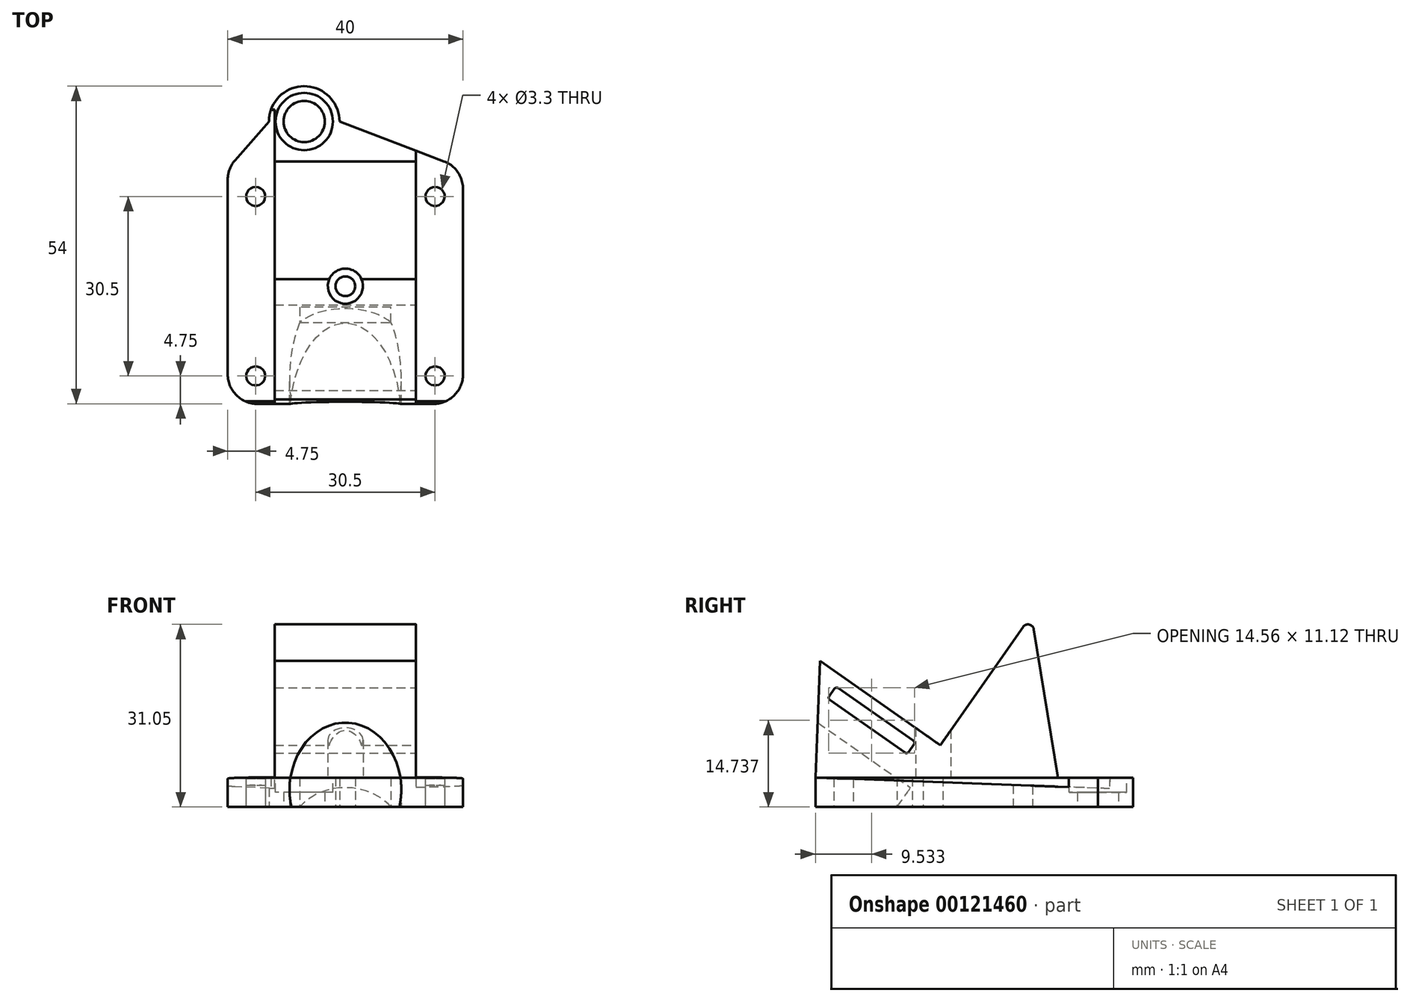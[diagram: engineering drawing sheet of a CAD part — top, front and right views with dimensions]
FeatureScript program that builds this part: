
annotation { "Feature Type Name" : "Feature", "Feature Type Description" : "" }
export const myFeature = defineFeature(function(context is Context, id is Id, definition is map)
    precondition{}
    {
        {
            var Q0;
            Q0=qCreatedBy(makeId("Top.planeOp"),FACE);
            var sketch = newSketch(context, id + "F0", { "sketchPlane" : qUnion([Q0])});
            skLineSegment(sketch, "E0.bottom", {"start": v(15.25, -15.25) * mm, "end": v(-15.25, -15.25) * mm, "construction": true});
            skLineSegment(sketch, "E0.top", {"start": v(15.25, 15.25) * mm, "end": v(-15.25, 15.25) * mm, "construction": true});
            skLineSegment(sketch, "E0.left", {"start": v(15.25, -15.25) * mm, "end": v(15.25, 15.25) * mm, "construction": true});
            skLineSegment(sketch, "E0.right", {"start": v(-15.25, -15.25) * mm, "end": v(-15.25, 15.25) * mm, "construction": true});
            skPoint(sketch, "E0.middle", {"position": v(0, 0) * mm});
            skCircle(sketch, "E1", {"center": v(-15.25, 15.25) * mm, "radius": 1.65 * mm});
            skCircle(sketch, "E2", {"center": v(15.25, 15.25) * mm, "radius": 1.65 * mm});
            skCircle(sketch, "E3", {"center": v(15.25, -15.25) * mm, "radius": 1.65 * mm});
            skCircle(sketch, "E4", {"center": v(-15.25, -15.25) * mm, "radius": 1.65 * mm});
            skLineSegment(sketch, "E5.bottom", {"start": v(15, -20) * mm, "end": v(-15, -20) * mm});
            skLineSegment(sketch, "E5.top", {"start": v(20, 20) * mm, "end": v(-20, 20) * mm});
            skLineSegment(sketch, "E5.left", {"start": v(20, -15) * mm, "end": v(20, 16.55) * mm});
            skLineSegment(sketch, "E5.right", {"start": v(-20, -15) * mm, "end": v(-20, 18.12) * mm});
            skCircle(sketch, "E6", {"center": v(-7, 28) * mm, "radius": 3.5 * mm});
            skPoint(sketch, "E6.centerSnap0", {"position": v(0, 20) * mm});
            skCircle(sketch, "E7", {"center": v(-7, 28) * mm, "radius": 6 * mm});
            skLineSegment(sketch, "E8", {"start": v(-13, 28) * mm, "end": v(-18.76, 21.41) * mm});
            skLineSegment(sketch, "E9", {"start": v(-1, 28) * mm, "end": v(16.78, 21.23) * mm});
            skPoint(sketch, "E10.visualSharp", {"position": v(-20, -20) * mm});
            skArc(sketch, "E10.filletArc", {"start": v(-20, -15) * mm, "mid": v(-18.54, -18.54) * mm, "end": v(-15, -20) * mm});
            skPoint(sketch, "E11.visualSharp", {"position": v(20, -20) * mm});
            skArc(sketch, "E11.filletArc", {"start": v(15, -20) * mm, "mid": v(18.54, -18.54) * mm, "end": v(20, -15) * mm});
            skPoint(sketch, "E12.visualSharp", {"position": v(20, 20) * mm});
            skArc(sketch, "E12.filletArc", {"start": v(20, 16.55) * mm, "mid": v(19.12, 19.4) * mm, "end": v(16.78, 21.23) * mm});
            skPoint(sketch, "E13.visualSharp", {"position": v(-20, 20) * mm});
            skArc(sketch, "E13.filletArc", {"start": v(-18.76, 21.41) * mm, "mid": v(-19.68, 19.88) * mm, "end": v(-20, 18.12) * mm});
            skSolve(sketch);
        }
        {
            var Q0;
            Q0 = qSketchRegion(id + "F0", true);
            extrude(context, id + "F1", {"entities" : qUnion([Q0]), "depth" : 5 * mm});
        }
        {
            var Q0;
            Q0=makeQuery(id+"F1.opExtrude","SWEPT_FACE",FACE,{"disambiguationData":[OSD([sQuery(id+"F0.wireOp",EDGE,"E5.left")])]});
            var sketch = newSketch(context, id + "F2", { "sketchPlane" : qUnion([Q0])});
            skLineSegment(sketch, "E14", {"start": v(-19.25, 24.86) * mm, "end": v(1.23, 10.52) * mm});
            skLineSegment(sketch, "E15", {"start": v(1.23, 10.52) * mm, "end": v(16.71, 32.63) * mm});
            skLineSegment(sketch, "E16", {"start": v(16.71, 32.63) * mm, "end": v(21.23, 5) * mm});
            skLineSegment(sketch, "E17", {"start": v(-19.25, 24.86) * mm, "end": v(-20, 5) * mm});
            skLineSegment(sketch, "E18", {"start": v(-16.1, 20.2) * mm, "end": v(-3.4, 11.32) * mm});
            skLineSegment(sketch, "E19", {"start": v(-3.28, 10.62) * mm, "end": v(-4.14, 9.4) * mm});
            skLineSegment(sketch, "E20", {"start": v(-4.84, 9.27) * mm, "end": v(-17.53, 18.16) * mm});
            skLineSegment(sketch, "E21", {"start": v(-17.66, 18.86) * mm, "end": v(-16.8, 20.08) * mm});
            skLineSegment(sketch, "E22", {"start": v(-20, 5) * mm, "end": v(21.23, 5) * mm});
            skPoint(sketch, "E23.visualSharp", {"position": v(-3, 11.03) * mm});
            skArc(sketch, "E23.filletArc", {"start": v(-3.28, 10.62) * mm, "mid": v(-3.2, 11) * mm, "end": v(-3.4, 11.32) * mm});
            skPoint(sketch, "E24.visualSharp", {"position": v(-4.43, 8.98) * mm});
            skArc(sketch, "E24.filletArc", {"start": v(-4.84, 9.27) * mm, "mid": v(-4.46, 9.19) * mm, "end": v(-4.14, 9.4) * mm});
            skPoint(sketch, "E25.visualSharp", {"position": v(-17.94, 18.45) * mm});
            skArc(sketch, "E25.filletArc", {"start": v(-17.66, 18.86) * mm, "mid": v(-17.74, 18.48) * mm, "end": v(-17.53, 18.16) * mm});
            skPoint(sketch, "E26.visualSharp", {"position": v(-16.5, 20.5) * mm});
            skArc(sketch, "E26.filletArc", {"start": v(-16.1, 20.2) * mm, "mid": v(-16.47, 20.29) * mm, "end": v(-16.8, 20.08) * mm});
            skSolve(sketch);
        }
        {
            var Q0;
            Q0 = qSketchRegion(id + "F2", true);
            extrude(context, id + "F3", {"entities" : qUnion([Q0]), "oppositeDirection" : true, "depth" : 40 * mm});
        }
        {
            var Q0;
            Q0=makeQuery(id+"F3.opExtrude","SWEPT_FACE",FACE,{"disambiguationData":[OSD([sQuery(id+"F2.wireOp",EDGE,"E15")])]});
            var sketch = newSketch(context, id + "F4", { "sketchPlane" : qUnion([Q0])});
            skCircle(sketch, "E27", {"center": v(0, -9) * mm, "radius": 9.5 * mm});
            skSolve(sketch);
        }
        {
            var Q0;
            Q0 = qSketchRegion(id + "F4", true);
            extrude(context, id + "F5", {"entities" : qUnion([Q0]), "operationType" : NewBodyOperationType.REMOVE, "depth" : 25 * mm});
        }
        {
            var Q0;
            Q0=makeQuery(id+"F1.opExtrude","CAP_FACE",FACE,{"disambiguationData":[OSD([sQuery(id+"F0.wireOp",EDGE,"E1"),sQuery(id+"F0.wireOp",EDGE,"E2"),sQuery(id+"F0.wireOp",EDGE,"E3"),sQuery(id+"F0.wireOp",EDGE,"E4"),sQuery(id+"F0.wireOp",EDGE,"E5.bottom"),sQuery(id+"F0.wireOp",EDGE,"E5.left"),sQuery(id+"F0.wireOp",EDGE,"E5.right"),sQuery(id+"F0.wireOp",EDGE,"E6"),sQuery(id+"F0.wireOp",EDGE,"E7"),sQuery(id+"F0.wireOp",EDGE,"E8"),sQuery(id+"F0.wireOp",EDGE,"E9"),sQuery(id+"F0.wireOp",EDGE,"E10.filletArc"),sQuery(id+"F0.wireOp",EDGE,"E11.filletArc"),sQuery(id+"F0.wireOp",EDGE,"E12.filletArc"),sQuery(id+"F0.wireOp",EDGE,"E13.filletArc")])],"isStart":false});
            var sketch = newSketch(context, id + "F6", { "sketchPlane" : qUnion([Q0])});
            skCircle(sketch, "E28", {"center": v(0, 0) * mm, "radius": 1.68 * mm});
            skSolve(sketch);
        }
        {
            var Q0;
            Q0 = qSketchRegion(id + "F6", true);
            extrude(context, id + "F7", {"entities" : qUnion([Q0]), "operationType" : NewBodyOperationType.REMOVE, "depth" : 25 * mm, "hasSecondDirection" : true, "secondDirectionOppositeDirection" : true, "secondDirectionDepth" : 25 * mm});
        }
        {
            var Q0;
            Q0=makeQuery(id+"F1.opExtrude","CAP_FACE",FACE,{"disambiguationData":[OSD([sQuery(id+"F0.wireOp",EDGE,"E1"),sQuery(id+"F0.wireOp",EDGE,"E2"),sQuery(id+"F0.wireOp",EDGE,"E3"),sQuery(id+"F0.wireOp",EDGE,"E4"),sQuery(id+"F0.wireOp",EDGE,"E5.bottom"),sQuery(id+"F0.wireOp",EDGE,"E5.left"),sQuery(id+"F0.wireOp",EDGE,"E5.right"),sQuery(id+"F0.wireOp",EDGE,"E6"),sQuery(id+"F0.wireOp",EDGE,"E7"),sQuery(id+"F0.wireOp",EDGE,"E8"),sQuery(id+"F0.wireOp",EDGE,"E9"),sQuery(id+"F0.wireOp",EDGE,"E10.filletArc"),sQuery(id+"F0.wireOp",EDGE,"E11.filletArc"),sQuery(id+"F0.wireOp",EDGE,"E12.filletArc"),sQuery(id+"F0.wireOp",EDGE,"E13.filletArc")])],"isStart":false});
            var sketch = newSketch(context, id + "F8", { "sketchPlane" : qUnion([Q0])});
            skCircle(sketch, "E29", {"center": v(-15.25, -15.25) * mm, "radius": 3 * mm});
            skCircle(sketch, "E30", {"center": v(-15.25, 15.25) * mm, "radius": 3 * mm});
            skCircle(sketch, "E31", {"center": v(15.25, 15.25) * mm, "radius": 3 * mm});
            skCircle(sketch, "E32", {"center": v(15.25, -15.25) * mm, "radius": 3 * mm});
            skCircle(sketch, "E33", {"center": v(0, 0) * mm, "radius": 3 * mm});
            skSolve(sketch);
        }
        {
            var Q0;
            Q0 = qSketchRegion(id + "F8", true);
            extrude(context, id + "F9", {"entities" : qUnion([Q0]), "operationType" : NewBodyOperationType.REMOVE, "depth" : 40 * mm});
        }
        {
            var Q0;
            Q0=makeQuery(id+"F1.opExtrude","CAP_FACE",FACE,{"disambiguationData":[OSD([sQuery(id+"F0.wireOp",EDGE,"E1"),sQuery(id+"F0.wireOp",EDGE,"E2"),sQuery(id+"F0.wireOp",EDGE,"E3"),sQuery(id+"F0.wireOp",EDGE,"E4"),sQuery(id+"F0.wireOp",EDGE,"E5.bottom"),sQuery(id+"F0.wireOp",EDGE,"E5.left"),sQuery(id+"F0.wireOp",EDGE,"E5.right"),sQuery(id+"F0.wireOp",EDGE,"E6"),sQuery(id+"F0.wireOp",EDGE,"E7"),sQuery(id+"F0.wireOp",EDGE,"E8"),sQuery(id+"F0.wireOp",EDGE,"E9"),sQuery(id+"F0.wireOp",EDGE,"E10.filletArc"),sQuery(id+"F0.wireOp",EDGE,"E11.filletArc"),sQuery(id+"F0.wireOp",EDGE,"E12.filletArc"),sQuery(id+"F0.wireOp",EDGE,"E13.filletArc")])],"isStart":true});
            var sketch = newSketch(context, id + "F10", { "sketchPlane" : qUnion([Q0])});
            skEllipticalArc(sketch, "E34.0.0", {});
            skLineSegment(sketch, "E34.0.1", {"start": v(7.76, 6.14) * mm, "end": v(-7.76, 6.14) * mm});
            skEllipticalArc(sketch, "E34.0.2", {});
            skLineSegment(sketch, "E34.0.3", {"start": v(-9.17, 20) * mm, "end": v(-15, 20) * mm});
            skArc(sketch, "E34.0.4", {"start": v(-15, 20) * mm, "mid": v(-18.54, 18.54) * mm, "end": v(-20, 15) * mm});
            skLineSegment(sketch, "E34.0.5", {"start": v(-20, 15) * mm, "end": v(-20, -18.12) * mm});
            skArc(sketch, "E34.0.6", {"start": v(-20, -18.12) * mm, "mid": v(-19.68, -19.88) * mm, "end": v(-18.76, -21.41) * mm});
            skLineSegment(sketch, "E34.0.7", {"start": v(-18.76, -21.41) * mm, "end": v(-13, -28) * mm});
            skArc(sketch, "E34.0.8", {"start": v(-13, -28) * mm, "mid": v(-7, -34) * mm, "end": v(-1, -28) * mm});
            skLineSegment(sketch, "E34.0.9", {"start": v(-1, -28) * mm, "end": v(16.78, -21.23) * mm});
            skArc(sketch, "E34.0.10", {"start": v(16.78, -21.23) * mm, "mid": v(19.12, -19.4) * mm, "end": v(20, -16.55) * mm});
            skLineSegment(sketch, "E34.0.11", {"start": v(20, -16.55) * mm, "end": v(20, 15) * mm});
            skArc(sketch, "E34.0.12", {"start": v(20, 15) * mm, "mid": v(18.54, 18.54) * mm, "end": v(15, 20) * mm});
            skLineSegment(sketch, "E34.0.13", {"start": v(15, 20) * mm, "end": v(9.17, 20) * mm});
            skLineSegment(sketch, "E35", {"start": v(20, 15) * mm, "end": v(20, 23.82) * mm});
            skLineSegment(sketch, "E36", {"start": v(20, 23.82) * mm, "end": v(15.3, 23.82) * mm});
            skLineSegment(sketch, "E37", {"start": v(15.3, 23.82) * mm, "end": v(15, 20) * mm});
            skLineSegment(sketch, "E38", {"start": v(-15, 20) * mm, "end": v(-18.4, 22.27) * mm});
            skLineSegment(sketch, "E39", {"start": v(-18.4, 22.27) * mm, "end": v(-22.44, 20.61) * mm});
            skLineSegment(sketch, "E40", {"start": v(-22.44, 20.61) * mm, "end": v(-20, 15) * mm});
            const initialGuessF10  = {"E34.0.0": [0, 0.015691021160589888, 0, -1, 0.01569102116058989, 0.009, 0.9365745042402244, 1.8489848879951825], "E34.0.2": [0, 0.015691021160589888, 0, -1, 0.01569102116058989, 0.009, 4.434200419184404, 5.346610802939362]};
            skSetInitialGuess(sketch, initialGuessF10);
            skSolve(sketch);
        }
        {
            var Q0;
            Q0=makeQuery(id+"F10.imprint","IMPRINT",FACE,{"disambiguationData":[TD([[makeQuery(id+"F10.imprint","IMPRINT",EDGE,{"derivedFrom":sQuery(id+"F10.wireOp",EDGE,"E34.0.4")}),1.0]])]});
            var Q1;
            Q1=makeQuery(id+"F10.imprint","IMPRINT",FACE,{"disambiguationData":[TD([[makeQuery(id+"F10.imprint","IMPRINT",EDGE,{"derivedFrom":sQuery(id+"F10.wireOp",EDGE,"E34.0.12")}),1.0]])]});
            extrude(context, id + "F11", {"entities" : qUnion([Q0, Q1]), "operationType" : NewBodyOperationType.REMOVE, "oppositeDirection" : true, "depth" : 40 * mm});
        }
        {
            var Q0;
            Q0=makeQuery(id+"F3.opExtrude","SWEPT_FACE",FACE,{"disambiguationData":[OSD([sQuery(id+"F2.wireOp",EDGE,"E17")])]});
            var sketch = newSketch(context, id + "F12", { "sketchPlane" : qUnion([Q0])});
            skLineSegment(sketch, "E41", {"start": v(12, 4.26) * mm, "end": v(12, 44.26) * mm});
            skLineSegment(sketch, "E42", {"start": v(-12, 44.26) * mm, "end": v(-12, 4.26) * mm});
            skLineSegment(sketch, "E43", {"start": v(-12, 4.26) * mm, "end": v(-20.56, 4.26) * mm});
            skLineSegment(sketch, "E44", {"start": v(-20.56, 4.26) * mm, "end": v(-20.56, 44.26) * mm});
            skLineSegment(sketch, "E45", {"start": v(-20.56, 44.26) * mm, "end": v(-12, 44.26) * mm});
            skLineSegment(sketch, "E46", {"start": v(12, 44.26) * mm, "end": v(21.16, 44.26) * mm});
            skLineSegment(sketch, "E47", {"start": v(21.16, 44.26) * mm, "end": v(21.16, 4.26) * mm});
            skLineSegment(sketch, "E48", {"start": v(21.16, 4.26) * mm, "end": v(12, 4.26) * mm});
            skSolve(sketch);
        }
        {
            var Q0;
            Q0 = qSketchRegion(id + "F12", true);
            extrude(context, id + "F13", {"entities" : qUnion([Q0]), "operationType" : NewBodyOperationType.REMOVE, "oppositeDirection" : true, "depth" : 50 * mm});
        }
        {
            var Q0;
            {var subQ0=sQuery(id+"F2.wireOp",EDGE,"E15");var subQ1=sQuery(id+"F2.wireOp",EDGE,"E16");Q0=makeQuery(id+"F9.boolean.opBoolean","SPLIT",EDGE,{"disambiguationData":[TD([makeQuery(id+"F3.opExtrude","SWEPT_FACE",FACE,{"disambiguationData":[OSD([subQ0])]}),makeQuery(id+"F3.opExtrude","SWEPT_FACE",FACE,{"disambiguationData":[OSD([subQ1])]}),makeQuery(id+"F9.opExtrude","SWEPT_FACE",FACE,{"disambiguationData":[OSD([sQuery(id+"F8.wireOp",EDGE,"E30")])]}),makeQuery(id+"F9.opExtrude","SWEPT_FACE",FACE,{"disambiguationData":[OSD([sQuery(id+"F8.wireOp",EDGE,"E31")])]})])],"derivedFrom":makeQuery(id+"F3.opExtrude","SWEPT_EDGE",EDGE,{"disambiguationData":[OSD([subQ0,subQ1])]})});}
            fillet(context, id + "F14", {"entities" : qUnion([Q0]), "radius" : 1 * mm, "tangentPropagation" : true, "allowEdgeOverflow" : false});
        }
        {
            var Q0;
            Q0=makeQuery(id+"F1.opExtrude","CAP_FACE",FACE,{"disambiguationData":[OSD([sQuery(id+"F0.wireOp",EDGE,"E1"),sQuery(id+"F0.wireOp",EDGE,"E2"),sQuery(id+"F0.wireOp",EDGE,"E3"),sQuery(id+"F0.wireOp",EDGE,"E4"),sQuery(id+"F0.wireOp",EDGE,"E5.bottom"),sQuery(id+"F0.wireOp",EDGE,"E5.left"),sQuery(id+"F0.wireOp",EDGE,"E5.right"),sQuery(id+"F0.wireOp",EDGE,"E6"),sQuery(id+"F0.wireOp",EDGE,"E7"),sQuery(id+"F0.wireOp",EDGE,"E8"),sQuery(id+"F0.wireOp",EDGE,"E9"),sQuery(id+"F0.wireOp",EDGE,"E10.filletArc"),sQuery(id+"F0.wireOp",EDGE,"E11.filletArc"),sQuery(id+"F0.wireOp",EDGE,"E12.filletArc"),sQuery(id+"F0.wireOp",EDGE,"E13.filletArc")])],"isStart":false});
            var sketch = newSketch(context, id + "F15", { "sketchPlane" : qUnion([Q0])});
            skCircle(sketch, "E49", {"center": v(-7, 28) * mm, "radius": 4.88 * mm});
            skSolve(sketch);
        }
        {
            var Q0;
            Q0 = qSketchRegion(id + "F15", true);
            extrude(context, id + "F16", {"entities" : qUnion([Q0]), "operationType" : NewBodyOperationType.REMOVE, "oppositeDirection" : true, "depth" : 2.5 * mm});
        }
        {
            var Q0;
            Q0=makeQuery(id+"F1.opExtrude","CAP_FACE",FACE,{"disambiguationData":[OSD([sQuery(id+"F0.wireOp",EDGE,"E1"),sQuery(id+"F0.wireOp",EDGE,"E2"),sQuery(id+"F0.wireOp",EDGE,"E3"),sQuery(id+"F0.wireOp",EDGE,"E4"),sQuery(id+"F0.wireOp",EDGE,"E5.bottom"),sQuery(id+"F0.wireOp",EDGE,"E5.left"),sQuery(id+"F0.wireOp",EDGE,"E5.right"),sQuery(id+"F0.wireOp",EDGE,"E6"),sQuery(id+"F0.wireOp",EDGE,"E7"),sQuery(id+"F0.wireOp",EDGE,"E8"),sQuery(id+"F0.wireOp",EDGE,"E9"),sQuery(id+"F0.wireOp",EDGE,"E10.filletArc"),sQuery(id+"F0.wireOp",EDGE,"E11.filletArc"),sQuery(id+"F0.wireOp",EDGE,"E12.filletArc"),sQuery(id+"F0.wireOp",EDGE,"E13.filletArc")])],"isStart":true});
            var sketch = newSketch(context, id + "F17", { "sketchPlane" : qUnion([Q0])});
            skLineSegment(sketch, "E50.0", {"start": v(-7.76, 6.14) * mm, "end": v(7.76, 6.14) * mm});
            skLineSegment(sketch, "E51", {"start": v(7.76, 6.14) * mm, "end": v(7.76, 3.57) * mm});
            skLineSegment(sketch, "E52", {"start": v(7.76, 3.57) * mm, "end": v(-7.76, 3.57) * mm});
            skLineSegment(sketch, "E53", {"start": v(-7.76, 3.57) * mm, "end": v(-7.76, 6.14) * mm});
            skSolve(sketch);
        }
        {
            var Q0;
            Q0 = qSketchRegion(id + "F17", true);
            extrude(context, id + "F18", {"entities" : qUnion([Q0]), "oppositeDirection" : true, "depth" : 5 * mm});
        }
    });
